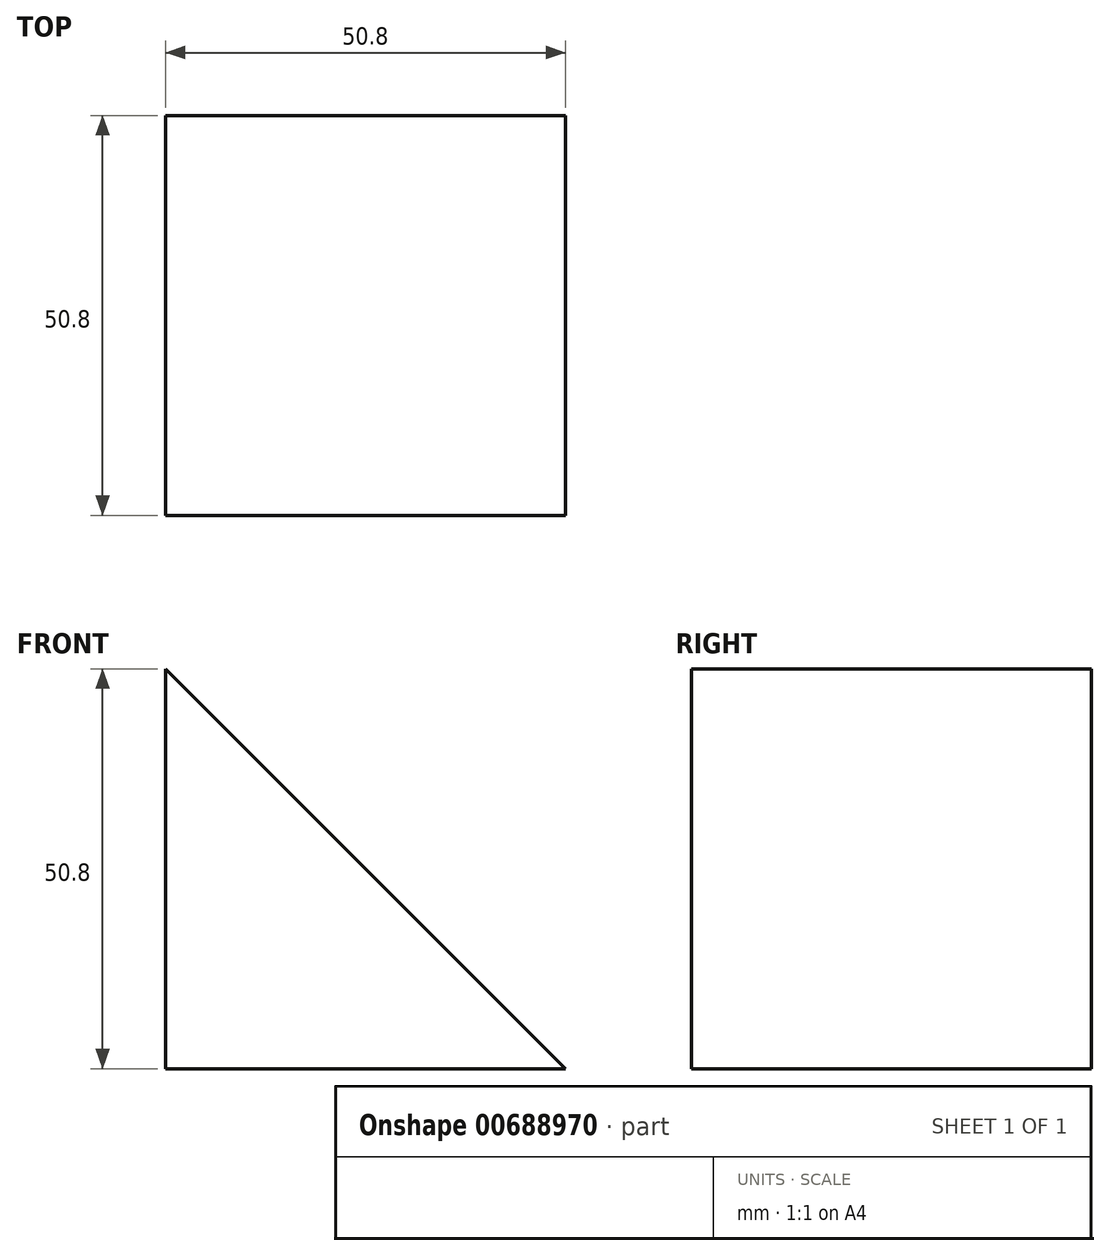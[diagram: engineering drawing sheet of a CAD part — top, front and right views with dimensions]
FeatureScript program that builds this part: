
annotation { "Feature Type Name" : "Feature", "Feature Type Description" : "" }
export const myFeature = defineFeature(function(context is Context, id is Id, definition is map)
    precondition{}
    {
        {
            var Q0;
            Q0=qCreatedBy(makeId("Front.planeOp"),FACE);
            var sketch = newSketch(context, id + "F0", { "sketchPlane" : qUnion([Q0])});
            skLineSegment(sketch, "E0", {"start": v(-55.66, 74) * mm, "end": v(-55.66, 23.2) * mm});
            skLineSegment(sketch, "E1", {"start": v(-55.66, 23.2) * mm, "end": v(-4.86, 23.2) * mm});
            skLineSegment(sketch, "E2", {"start": v(-55.66, 74) * mm, "end": v(-4.86, 23.2) * mm});
            skSolve(sketch);
        }
        {
            var Q0;
            Q0=makeQuery(id+"F0.imprint","IMPRINT",FACE,{"disambiguationData":[TD([[makeQuery(id+"F0.imprint","IMPRINT",EDGE,{"derivedFrom":sQuery(id+"F0.wireOp",EDGE,"E0")}),1.0]])]});
            extrude(context, id + "F1", {"entities" : qUnion([Q0]), "depth" : 50.8 * mm, "offsetDistance" : 25.4 * mm});
        }
    });
